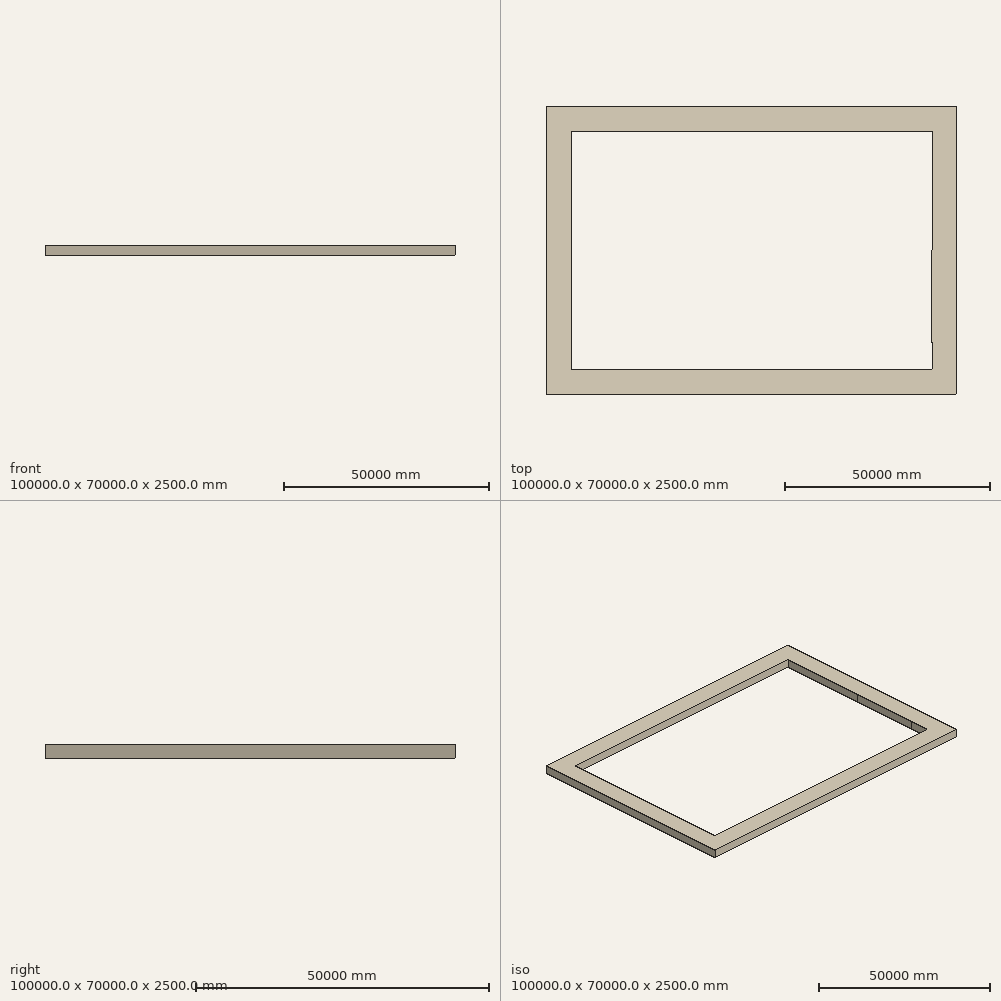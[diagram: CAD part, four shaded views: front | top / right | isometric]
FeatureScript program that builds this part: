
annotation { "Feature Type Name" : "Feature", "Feature Type Description" : "" }
export const myFeature = defineFeature(function(context is Context, id is Id, definition is map)
    precondition{}
    {
        {
            var Q0;
            Q0=qCreatedBy(makeId("Top.planeOp"),FACE);
            var sketch = newSketch(context, id + "F0", { "sketchPlane" : qUnion([Q0])});
            skLineSegment(sketch, "E0.bottom", {"start": v(-71.7, 69952.59) * mm, "end": v(99928.3, 69952.59) * mm});
            skLineSegment(sketch, "E0.top", {"start": v(-71.7, -47.41) * mm, "end": v(99928.3, -47.41) * mm});
            skLineSegment(sketch, "E0.left", {"start": v(-71.7, 69952.59) * mm, "end": v(-71.7, -47.41) * mm});
            skLineSegment(sketch, "E0.right", {"start": v(99928.3, 69952.59) * mm, "end": v(99928.3, -47.41) * mm});
            skLineSegment(sketch, "E1.bottom", {"start": v(-71.7, 54784.83) * mm, "end": v(5928.3, 54784.83) * mm});
            skLineSegment(sketch, "E1.top", {"start": v(-71.7, 20165.76) * mm, "end": v(5928.3, 20165.76) * mm});
            skLineSegment(sketch, "E1.left", {"start": v(-71.7, 54784.83) * mm, "end": v(-71.7, 20165.76) * mm});
            skLineSegment(sketch, "E1.right", {"start": v(5928.3, 54784.83) * mm, "end": v(5928.3, 20165.76) * mm});
            skLineSegment(sketch, "E2.bottom", {"start": v(16766.25, 69952.59) * mm, "end": v(53913.67, 69952.59) * mm});
            skLineSegment(sketch, "E2.top", {"start": v(16766.25, 63952.59) * mm, "end": v(53913.67, 63952.59) * mm});
            skLineSegment(sketch, "E2.left", {"start": v(16766.25, 69952.59) * mm, "end": v(16766.25, 63952.59) * mm});
            skLineSegment(sketch, "E2.right", {"start": v(53913.67, 69952.59) * mm, "end": v(53913.67, 63952.59) * mm});
            skLineSegment(sketch, "E3.bottom", {"start": v(12098.5, -47.41) * mm, "end": v(33297.82, -47.41) * mm});
            skLineSegment(sketch, "E3.top", {"start": v(12098.5, 5952.59) * mm, "end": v(33297.82, 5952.59) * mm});
            skLineSegment(sketch, "E3.left", {"start": v(12098.5, -47.41) * mm, "end": v(12098.5, 5952.59) * mm});
            skLineSegment(sketch, "E3.right", {"start": v(33297.82, -47.41) * mm, "end": v(33297.82, 5952.59) * mm});
            skLineSegment(sketch, "E4.bottom", {"start": v(68889.34, -47.41) * mm, "end": v(91061.1, -47.41) * mm});
            skLineSegment(sketch, "E4.top", {"start": v(68889.34, 5952.59) * mm, "end": v(91061.1, 5952.59) * mm});
            skLineSegment(sketch, "E4.left", {"start": v(68889.34, -47.41) * mm, "end": v(68889.34, 5952.59) * mm});
            skLineSegment(sketch, "E4.right", {"start": v(91061.1, -47.41) * mm, "end": v(91061.1, 5952.59) * mm});
            skPoint(sketch, "E5.oppositeSnap0", {"position": v(99928.3, 34952.59) * mm});
            skLineSegment(sketch, "E5.bottom", {"start": v(99928.3, 12580.69) * mm, "end": v(93928.3, 12580.69) * mm});
            skLineSegment(sketch, "E5.top", {"start": v(99928.3, 34952.59) * mm, "end": v(93928.3, 34952.59) * mm});
            skLineSegment(sketch, "E5.left", {"start": v(99928.3, 12580.69) * mm, "end": v(99928.3, 34952.59) * mm});
            skLineSegment(sketch, "E5.right", {"start": v(93928.3, 12580.69) * mm, "end": v(93928.3, 34952.59) * mm});
            skLineSegment(sketch, "E6.bottom", {"start": v(89116.21, 69952.59) * mm, "end": v(70639.74, 69952.59) * mm});
            skLineSegment(sketch, "E6.top", {"start": v(89116.21, 63952.59) * mm, "end": v(70639.74, 63952.59) * mm});
            skLineSegment(sketch, "E6.left", {"start": v(89116.21, 69952.59) * mm, "end": v(89116.21, 63952.59) * mm});
            skLineSegment(sketch, "E6.right", {"start": v(70639.74, 69952.59) * mm, "end": v(70639.74, 63952.59) * mm});
            skLineSegment(sketch, "E7.bottom", {"start": v(94021.76, 6009.93) * mm, "end": v(5928.3, 6009.93) * mm});
            skLineSegment(sketch, "E7.top", {"start": v(94021.76, 63880.46) * mm, "end": v(5928.3, 63880.46) * mm});
            skLineSegment(sketch, "E7.left", {"start": v(94021.76, 6009.93) * mm, "end": v(94021.76, 63880.46) * mm});
            skLineSegment(sketch, "E7.right", {"start": v(5928.3, 6009.93) * mm, "end": v(5928.3, 63880.46) * mm});
            skLineSegment(sketch, "E8.bottom", {"start": v(94021.76, 59285.28) * mm, "end": v(99928.3, 59285.28) * mm});
            skLineSegment(sketch, "E8.top", {"start": v(94021.76, 52105.32) * mm, "end": v(99928.3, 52105.32) * mm});
            skLineSegment(sketch, "E8.left", {"start": v(94021.76, 59285.28) * mm, "end": v(94021.76, 52105.32) * mm});
            skLineSegment(sketch, "E8.right", {"start": v(99928.3, 59285.28) * mm, "end": v(99928.3, 52105.32) * mm});
            skSolve(sketch);
        }
        {
            var Q0;
            {var subQ4=sQuery(id+"F0.wireOp",EDGE,"E1.bottom");Q0=makeQuery(id+"F0.imprint","IMPRINT",FACE,{"disambiguationData":[TD([[makeQuery(id+"F0.imprint","IMPRINT",EDGE,{"derivedFrom":subQ4}),1.0]])]});}
            var Q1;
            {var subQ0=sQuery(id+"F0.wireOp",EDGE,"E5.top");var subQ1=sQuery(id+"F0.wireOp",EDGE,"E0.right");var subQ2=makeQuery(id+"F0.imprint","INTERSECT",VERTEX,{"derivedFrom":[subQ1,subQ0]});Q1=makeQuery(id+"F0.imprint","IMPRINT",FACE,{"disambiguationData":[TD([[makeQuery(id+"F0.imprint","IMPRINT",EDGE,{"disambiguationData":[TD([[subQ2,-1.0]])],"derivedFrom":subQ1}),-1.0]])]});}
            var Q2;
            {var subQ3=sQuery(id+"F0.wireOp",EDGE,"E8.top");Q2=makeQuery(id+"F0.imprint","IMPRINT",FACE,{"disambiguationData":[TD([[makeQuery(id+"F0.imprint","IMPRINT",EDGE,{"derivedFrom":subQ3}),-1.0]])]});}
            var Q3;
            {var subQ9=sQuery(id+"F0.wireOp",EDGE,"E1.top");Q3=makeQuery(id+"F0.imprint","IMPRINT",FACE,{"disambiguationData":[TD([[makeQuery(id+"F0.imprint","IMPRINT",EDGE,{"derivedFrom":subQ9}),-1.0]])]});}
            var Q4;
            {var subQ2=sQuery(id+"F0.wireOp",EDGE,"E8.bottom");Q4=makeQuery(id+"F0.imprint","IMPRINT",FACE,{"disambiguationData":[TD([[makeQuery(id+"F0.imprint","IMPRINT",EDGE,{"derivedFrom":subQ2}),-1.0]])]});}
            var Q5;
            Q5=makeQuery(id+"F0.imprint","IMPRINT",FACE,{"disambiguationData":[TD([[makeQuery(id+"F0.imprint","IMPRINT",EDGE,{"derivedFrom":sQuery(id+"F0.wireOp",EDGE,"E4.top")}),-1.0]])]});
            var Q6;
            Q6=makeQuery(id+"F0.imprint","IMPRINT",FACE,{"disambiguationData":[TD([[makeQuery(id+"F0.imprint","IMPRINT",EDGE,{"derivedFrom":sQuery(id+"F0.wireOp",EDGE,"E6.top")}),-1.0]])]});
            var Q7;
            Q7=makeQuery(id+"F0.imprint","IMPRINT",FACE,{"disambiguationData":[TD([[makeQuery(id+"F0.imprint","IMPRINT",EDGE,{"derivedFrom":sQuery(id+"F0.wireOp",EDGE,"E3.top")}),-1.0]])]});
            var Q8;
            Q8=makeQuery(id+"F0.imprint","IMPRINT",FACE,{"disambiguationData":[TD([[makeQuery(id+"F0.imprint","IMPRINT",EDGE,{"derivedFrom":sQuery(id+"F0.wireOp",EDGE,"E2.top")}),1.0]])]});
            var Q9;
            {var subQ0=sQuery(id+"F0.wireOp",EDGE,"E1.bottom");Q9=makeQuery(id+"F0.imprint","IMPRINT",FACE,{"disambiguationData":[TD([[makeQuery(id+"F0.imprint","IMPRINT",EDGE,{"derivedFrom":subQ0}),-1.0]])]});}
            var Q10;
            {var subQ0=sQuery(id+"F0.wireOp",EDGE,"E5.right");Q10=makeQuery(id+"F0.imprint","IMPRINT",FACE,{"disambiguationData":[TD([[makeQuery(id+"F0.imprint","IMPRINT",EDGE,{"derivedFrom":subQ0}),-1.0]])]});}
            extrude(context, id + "F1", {"entities" : qUnion([Q0, Q1, Q2, Q3, Q4, Q5, Q6, Q7, Q8, Q9, Q10]), "depth" : 2500 * mm, "offsetDistance" : 25 * mm});
        }
    });
